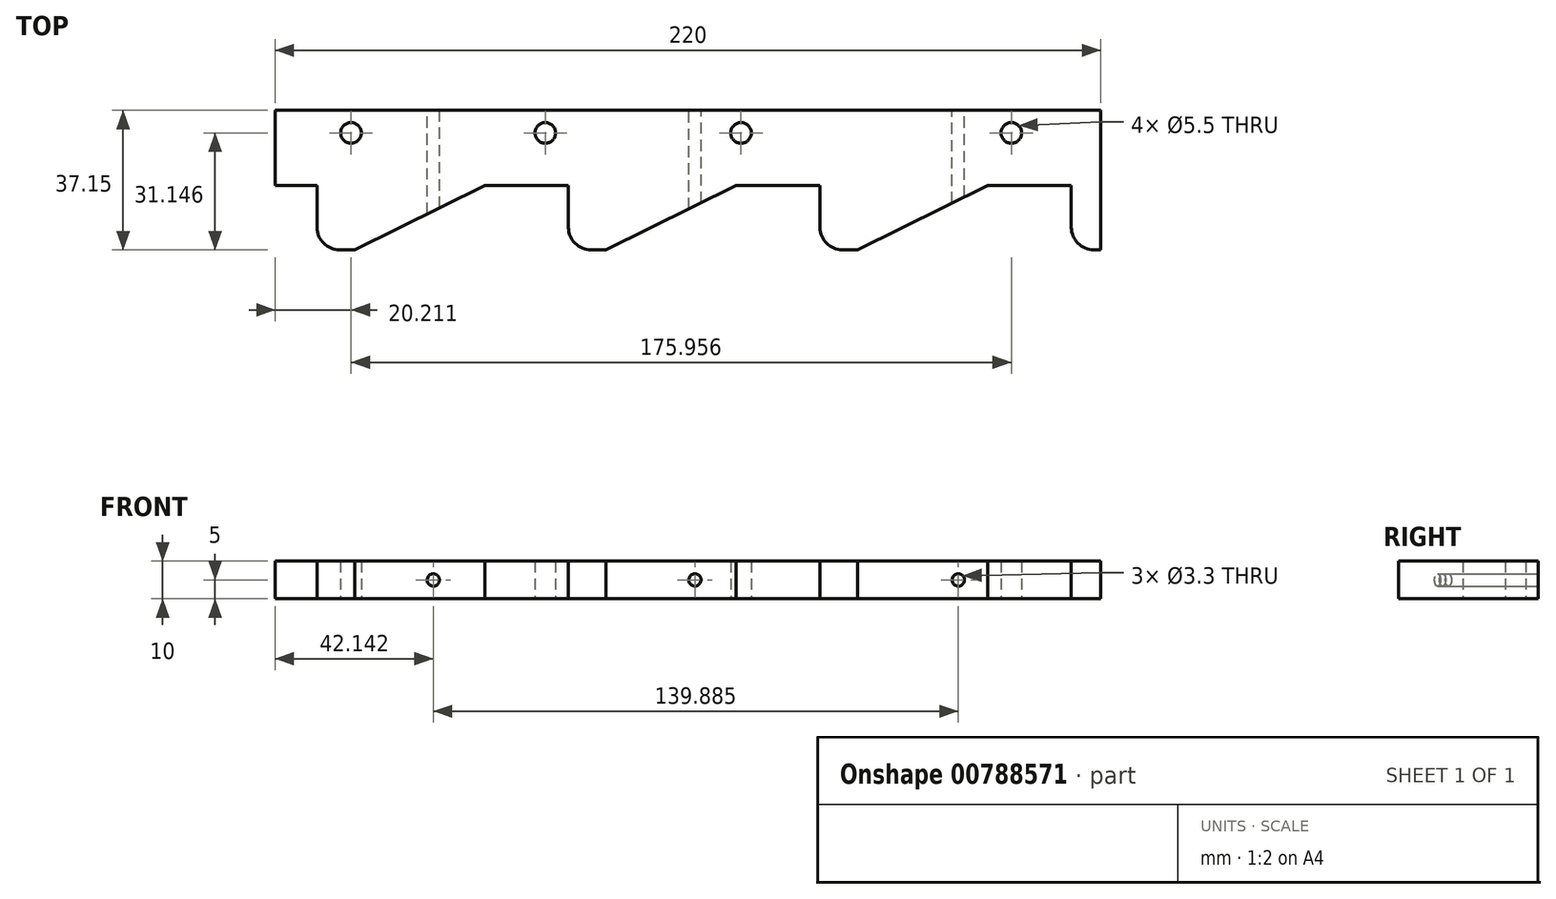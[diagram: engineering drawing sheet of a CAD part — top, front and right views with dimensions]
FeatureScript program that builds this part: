
annotation { "Feature Type Name" : "Feature", "Feature Type Description" : "" }
export const myFeature = defineFeature(function(context is Context, id is Id, definition is map)
    precondition{}
    {
        {
            var Q0;
            Q0=qCreatedBy(makeId("Top.planeOp"),FACE);
            var sketch = newSketch(context, id + "F0", { "sketchPlane" : qUnion([Q0])});
            skCircle(sketch, "E0.cCircle", {"center": v(0, 0) * mm, "radius": 58.02 * mm, "construction": true});
            skLineSegment(sketch, "E0.0", {"start": v(33.5, -58.02) * mm, "end": v(-33.5, -58.02) * mm, "construction": true});
            skLineSegment(sketch, "E0.1", {"start": v(-33.5, -58.02) * mm, "end": v(-67, 0) * mm});
            skLineSegment(sketch, "E0.2", {"start": v(-67, 0) * mm, "end": v(-33.5, 58.02) * mm});
            skLineSegment(sketch, "E0.3", {"start": v(-33.5, 58.02) * mm, "end": v(33.5, 58.02) * mm});
            skLineSegment(sketch, "E0.4", {"start": v(33.5, 58.02) * mm, "end": v(67, 0) * mm});
            skLineSegment(sketch, "E0.5", {"start": v(67, 0) * mm, "end": v(33.5, -58.02) * mm, "construction": true});
            skPoint(sketch, "E0.0.midPoint", {"position": v(0, -58.02) * mm});
            skCircle(sketch, "E1", {"center": v(-33.5, -58.02) * mm, "radius": 11.15 * mm});
            skCircle(sketch, "E2", {"center": v(33.5, -58.02) * mm, "radius": 11.15 * mm});
            skLineSegment(sketch, "E3", {"start": v(33.5, -58.02) * mm, "end": v(293.18, -58.02) * mm, "construction": true});
            skCircle(sketch, "E4", {"center": v(100.5, -58.02) * mm, "radius": 11.15 * mm});
            skCircle(sketch, "E5", {"center": v(167.5, -58.02) * mm, "radius": 11.15 * mm});
            skCircle(sketch, "E6", {"center": v(234.5, -58.02) * mm, "radius": 11.15 * mm});
            skLineSegment(sketch, "E7", {"start": v(111.65, -58.02) * mm, "end": v(111.65, -58.02) * mm});
            skLineSegment(sketch, "E8", {"start": v(178.65, -58.02) * mm, "end": v(178.65, -58.02) * mm});
            skLineSegment(sketch, "E9", {"start": v(44.65, -58.02) * mm, "end": v(44.65, -58.02) * mm});
            skLineSegment(sketch, "E10", {"start": v(-22.35, -58.02) * mm, "end": v(-22.35, -58.02) * mm});
            skLineSegment(sketch, "E11", {"start": v(33.5, -46.87) * mm, "end": v(44.65, -46.87) * mm});
            skLineSegment(sketch, "E12", {"start": v(44.65, -46.87) * mm, "end": v(44.65, -58.02) * mm});
            skLineSegment(sketch, "E13", {"start": v(33.5, -46.87) * mm, "end": v(22.35, -46.87) * mm});
            skLineSegment(sketch, "E14", {"start": v(22.35, -46.87) * mm, "end": v(-12.35, -64.02) * mm});
            skLineSegment(sketch, "E15", {"start": v(-12.35, -64.02) * mm, "end": v(-16.35, -64.02) * mm});
            skLineSegment(sketch, "E16.bottom", {"start": v(111.65, -58.02) * mm, "end": v(89.35, -58.02) * mm});
            skLineSegment(sketch, "E16.top", {"start": v(111.65, -46.87) * mm, "end": v(89.35, -46.87) * mm});
            skLineSegment(sketch, "E16.left", {"start": v(111.65, -58.02) * mm, "end": v(111.65, -46.87) * mm});
            skLineSegment(sketch, "E16.right", {"start": v(89.35, -58.02) * mm, "end": v(89.35, -46.87) * mm});
            skLineSegment(sketch, "E17", {"start": v(50.65, -64.02) * mm, "end": v(54.65, -64.02) * mm});
            skLineSegment(sketch, "E18", {"start": v(54.65, -64.02) * mm, "end": v(89.35, -46.87) * mm});
            skLineSegment(sketch, "E19.bottom", {"start": v(178.65, -58.02) * mm, "end": v(156.35, -58.02) * mm});
            skLineSegment(sketch, "E19.top", {"start": v(178.65, -46.87) * mm, "end": v(156.35, -46.87) * mm});
            skLineSegment(sketch, "E19.left", {"start": v(178.65, -58.02) * mm, "end": v(178.65, -46.87) * mm});
            skLineSegment(sketch, "E19.right", {"start": v(156.35, -58.02) * mm, "end": v(156.35, -46.87) * mm});
            skLineSegment(sketch, "E20.bottom", {"start": v(245.65, -58.02) * mm, "end": v(223.35, -58.02) * mm});
            skLineSegment(sketch, "E20.top", {"start": v(245.65, -46.87) * mm, "end": v(223.35, -46.87) * mm});
            skLineSegment(sketch, "E20.left", {"start": v(245.65, -58.02) * mm, "end": v(245.65, -46.87) * mm});
            skLineSegment(sketch, "E20.right", {"start": v(223.35, -58.02) * mm, "end": v(223.35, -46.87) * mm});
            skLineSegment(sketch, "E21", {"start": v(-22.35, -64.02) * mm, "end": v(-110.66, -64.02) * mm});
            skLineSegment(sketch, "E22", {"start": v(-109.7, -26.87) * mm, "end": v(271.3, -26.87) * mm});
            skLineSegment(sketch, "E23", {"start": v(271.3, -26.87) * mm, "end": v(271.3, -58.02) * mm});
            skLineSegment(sketch, "E24", {"start": v(117.65, -64.02) * mm, "end": v(121.65, -64.02) * mm});
            skLineSegment(sketch, "E25", {"start": v(121.65, -64.02) * mm, "end": v(156.35, -46.87) * mm});
            skLineSegment(sketch, "E26", {"start": v(184.65, -64.02) * mm, "end": v(188.65, -64.02) * mm});
            skLineSegment(sketch, "E27", {"start": v(188.65, -64.02) * mm, "end": v(223.35, -46.87) * mm});
            skPoint(sketch, "E28.visualSharp", {"position": v(44.65, -64.02) * mm});
            skArc(sketch, "E28.filletArc", {"start": v(44.65, -58.02) * mm, "mid": v(46.4, -62.27) * mm, "end": v(50.65, -64.02) * mm});
            skPoint(sketch, "E29.visualSharp", {"position": v(111.65, -64.02) * mm});
            skArc(sketch, "E29.filletArc", {"start": v(111.65, -58.02) * mm, "mid": v(113.4, -62.27) * mm, "end": v(117.65, -64.02) * mm});
            skPoint(sketch, "E30.visualSharp", {"position": v(178.65, -64.02) * mm});
            skArc(sketch, "E30.filletArc", {"start": v(178.65, -58.02) * mm, "mid": v(180.4, -62.27) * mm, "end": v(184.65, -64.02) * mm});
            skPoint(sketch, "E31.visualSharp", {"position": v(-22.35, -64.02) * mm});
            skArc(sketch, "E31.filletArc", {"start": v(-22.35, -58.02) * mm, "mid": v(-20.6, -62.27) * mm, "end": v(-16.35, -64.02) * mm});
            skLineSegment(sketch, "E32", {"start": v(245.65, -58.02) * mm, "end": v(245.65, -58.02) * mm});
            skLineSegment(sketch, "E33", {"start": v(251.65, -64.02) * mm, "end": v(269.26, -64.02) * mm});
            skLineSegment(sketch, "E34", {"start": v(269.26, -64.02) * mm, "end": v(271.3, -58.02) * mm});
            skPoint(sketch, "E35.visualSharp", {"position": v(245.65, -64.02) * mm});
            skArc(sketch, "E35.filletArc", {"start": v(245.65, -58.02) * mm, "mid": v(247.4, -62.27) * mm, "end": v(251.65, -64.02) * mm});
            skLineSegment(sketch, "E36", {"start": v(-109.7, -26.87) * mm, "end": v(-110.66, -64.02) * mm});
            skLineSegment(sketch, "E37", {"start": v(-16.35, -64.02) * mm, "end": v(-22.35, -64.02) * mm});
            skLineSegment(sketch, "E38.bottom", {"start": v(33.5, -78.5) * mm, "end": v(253.5, -78.5) * mm});
            skLineSegment(sketch, "E38.top", {"start": v(33.5, -15.68) * mm, "end": v(253.5, -15.68) * mm});
            skLineSegment(sketch, "E38.left", {"start": v(33.5, -78.5) * mm, "end": v(33.5, -15.68) * mm});
            skLineSegment(sketch, "E38.right", {"start": v(253.5, -78.5) * mm, "end": v(253.5, -15.68) * mm});
            skCircle(sketch, "E39", {"center": v(53.71, -32.87) * mm, "radius": 2.75 * mm});
            skCircle(sketch, "E40", {"center": v(105.48, -32.87) * mm, "radius": 2.75 * mm});
            skCircle(sketch, "E41", {"center": v(157.64, -32.87) * mm, "radius": 2.75 * mm});
            skCircle(sketch, "E42", {"center": v(229.67, -32.87) * mm, "radius": 2.75 * mm});
            skCircle(sketch, "E43", {"center": v(258.46, -32.87) * mm, "radius": 2.75 * mm});
            skSolve(sketch);
        }
        {
            var Q0;
            {var subQ13=sQuery(id+"F0.wireOp",EDGE,"E11");Q0=makeQuery(id+"F0.imprint","IMPRINT",FACE,{"disambiguationData":[TD([[makeQuery(id+"F0.imprint","IMPRINT",EDGE,{"derivedFrom":subQ13}),1.0]])]});}
            extrude(context, id + "F1", {"entities" : qUnion([Q0]), "depth" : 10 * mm, "offsetDistance" : 25 * mm});
        }
        {
            var Q0;
            Q0=makeQuery(id+"F1.opExtrude","SWEPT_FACE",FACE,{"disambiguationData":[OSD([sQuery(id+"F0.wireOp",EDGE,"E22")])]});
            var sketch = newSketch(context, id + "F2", { "sketchPlane" : qUnion([Q0])});
            skLineSegment(sketch, "E44", {"start": v(-253.5, 5) * mm, "end": v(-33.5, 5) * mm, "construction": true});
            skCircle(sketch, "E45", {"center": v(-215.53, 5) * mm, "radius": 1.65 * mm});
            skCircle(sketch, "E46", {"center": v(-145.34, 5) * mm, "radius": 1.65 * mm});
            skCircle(sketch, "E47", {"center": v(-75.64, 5) * mm, "radius": 1.65 * mm});
            skSolve(sketch);
        }
        {
            var Q0;
            Q0=makeQuery(id+"F2.imprint","IMPRINT",FACE,{"disambiguationData":[TD([[makeQuery(id+"F2.imprint","IMPRINT",EDGE,{"derivedFrom":sQuery(id+"F2.wireOp",EDGE,"E47")}),1.0]])]});
            var Q1;
            Q1=makeQuery(id+"F2.imprint","IMPRINT",FACE,{"disambiguationData":[TD([[makeQuery(id+"F2.imprint","IMPRINT",EDGE,{"derivedFrom":sQuery(id+"F2.wireOp",EDGE,"E46")}),1.0]])]});
            var Q2;
            Q2=makeQuery(id+"F2.imprint","IMPRINT",FACE,{"disambiguationData":[TD([[makeQuery(id+"F2.imprint","IMPRINT",EDGE,{"derivedFrom":sQuery(id+"F2.wireOp",EDGE,"E45")}),1.0]])]});
            extrude(context, id + "F3", {"entities" : qUnion([Q0, Q1, Q2]), "operationType" : NewBodyOperationType.REMOVE, "oppositeDirection" : true, "depth" : 47 * mm, "offsetDistance" : 25 * mm});
        }
    });
